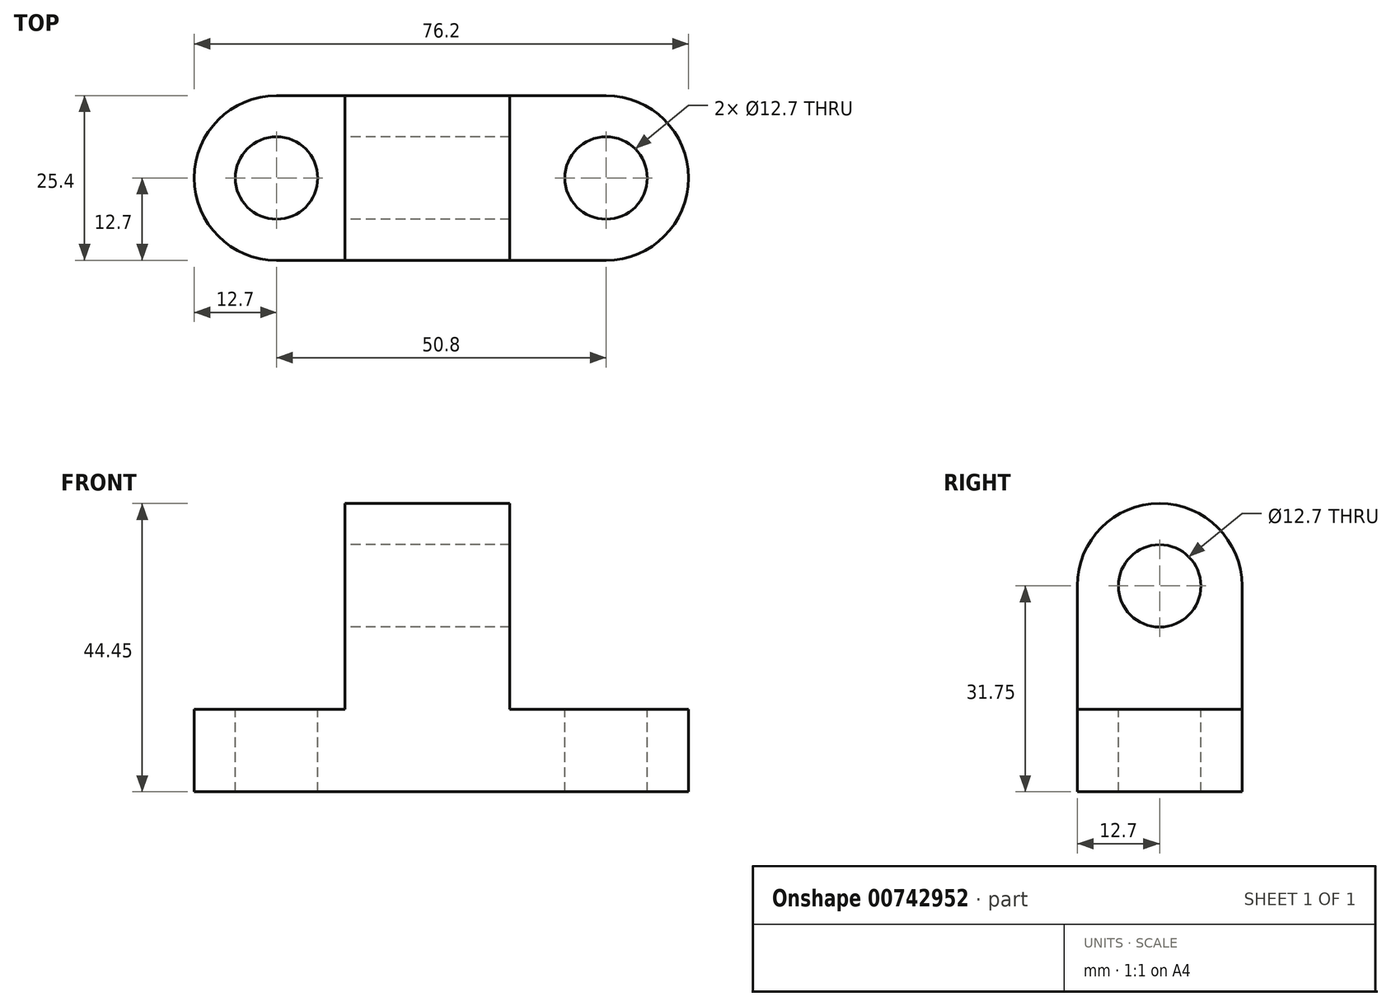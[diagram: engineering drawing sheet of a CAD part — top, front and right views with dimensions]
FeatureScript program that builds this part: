
annotation { "Feature Type Name" : "Feature", "Feature Type Description" : "" }
export const myFeature = defineFeature(function(context is Context, id is Id, definition is map)
    precondition{}
    {
        {
            var Q0;
            Q0=qCreatedBy(makeId("Front.planeOp"),FACE);
            var sketch = newSketch(context, id + "F0", { "sketchPlane" : qUnion([Q0])});
            skLineSegment(sketch, "E0.bottom", {"start": v(0, 0) * mm, "end": v(76.2, 0) * mm});
            skLineSegment(sketch, "E0.top", {"start": v(0, 57.15) * mm, "end": v(76.2, 57.15) * mm});
            skLineSegment(sketch, "E0.left", {"start": v(0, 0) * mm, "end": v(0, 57.15) * mm});
            skLineSegment(sketch, "E0.right", {"start": v(76.2, 0) * mm, "end": v(76.2, 57.15) * mm});
            skSolve(sketch);
        }
        {
            var Q0;
            Q0=makeQuery(id+"F0.imprint","IMPRINT",FACE,{"disambiguationData":[TD([[makeQuery(id+"F0.imprint","IMPRINT",EDGE,{"derivedFrom":sQuery(id+"F0.wireOp",EDGE,"E0.bottom")}),1.0]])]});
            extrude(context, id + "F1", {"entities" : qUnion([Q0]), "depth" : 25.4 * mm, "offsetDistance" : 25.4 * mm});
        }
        {
            var Q0;
            Q0=makeQuery(id+"F1.opExtrude","CAP_FACE",FACE,{"disambiguationData":[OSD([sQuery(id+"F0.wireOp",EDGE,"E0.bottom"),sQuery(id+"F0.wireOp",EDGE,"E0.top"),sQuery(id+"F0.wireOp",EDGE,"E0.left"),sQuery(id+"F0.wireOp",EDGE,"E0.right")])],"isStart":false});
            var sketch = newSketch(context, id + "F2", { "sketchPlane" : qUnion([Q0])});
            skLineSegment(sketch, "E1", {"start": v(0, 44.45) * mm, "end": v(76.2, 44.45) * mm});
            skLineSegment(sketch, "E2", {"start": v(76.2, 44.45) * mm, "end": v(76.2, 57.15) * mm});
            skLineSegment(sketch, "E3", {"start": v(76.2, 57.15) * mm, "end": v(0, 57.15) * mm});
            skLineSegment(sketch, "E4", {"start": v(0, 57.15) * mm, "end": v(0, 44.45) * mm});
            skSolve(sketch);
        }
        {
            var Q0;
            Q0 = qSketchRegion(id + "F2", true);
            extrude(context, id + "F3", {"entities" : qUnion([Q0]), "operationType" : NewBodyOperationType.REMOVE, "oppositeDirection" : true, "depth" : 25.4 * mm, "offsetDistance" : 25.4 * mm});
        }
        {
            var Q0;
            Q0=makeQuery(id+"F3.boolean.opBoolean","COPY",FACE,{"derivedFrom":makeQuery(id+"F3.opExtrude","SWEPT_FACE",FACE,{"disambiguationData":[OSD([sQuery(id+"F2.wireOp",EDGE,"E1")])]})});
            var sketch = newSketch(context, id + "F4", { "sketchPlane" : qUnion([Q0])});
            skLineSegment(sketch, "E5", {"start": v(48.66, 0) * mm, "end": v(76.2, 0) * mm});
            skLineSegment(sketch, "E6", {"start": v(76.2, 0) * mm, "end": v(76.2, -25.4) * mm});
            skLineSegment(sketch, "E7", {"start": v(76.2, -25.4) * mm, "end": v(48.66, -25.4) * mm});
            skLineSegment(sketch, "E8", {"start": v(48.66, -25.4) * mm, "end": v(48.66, 0) * mm});
            skLineSegment(sketch, "E9", {"start": v(23.26, 0) * mm, "end": v(23.26, -25.4) * mm});
            skLineSegment(sketch, "E10", {"start": v(23.26, -25.4) * mm, "end": v(0, -25.4) * mm});
            skLineSegment(sketch, "E11", {"start": v(0, -25.4) * mm, "end": v(0, 0) * mm});
            skLineSegment(sketch, "E12", {"start": v(0, 0) * mm, "end": v(23.26, 0) * mm});
            skSolve(sketch);
        }
        {
            var Q0;
            Q0=makeQuery(id+"F4.imprint","IMPRINT",FACE,{"disambiguationData":[TD([[makeQuery(id+"F4.imprint","IMPRINT",EDGE,{"derivedFrom":sQuery(id+"F4.wireOp",EDGE,"E9")}),-1.0]])]});
            var Q1;
            Q1=makeQuery(id+"F4.imprint","IMPRINT",FACE,{"disambiguationData":[TD([[makeQuery(id+"F4.imprint","IMPRINT",EDGE,{"derivedFrom":sQuery(id+"F4.wireOp",EDGE,"E5")}),-1.0]])]});
            extrude(context, id + "F5", {"entities" : qUnion([Q0, Q1]), "operationType" : NewBodyOperationType.REMOVE, "oppositeDirection" : true, "depth" : 31.75 * mm, "offsetDistance" : 25.4 * mm});
        }
        {
            var Q0;
            Q0=makeQuery(id+"F5.boolean.opBoolean","COPY",FACE,{"derivedFrom":makeQuery(id+"F5.opExtrude","CAP_FACE",FACE,{"disambiguationData":[OSD([sQuery(id+"F4.wireOp",EDGE,"E5"),sQuery(id+"F4.wireOp",EDGE,"E6"),sQuery(id+"F4.wireOp",EDGE,"E7"),sQuery(id+"F4.wireOp",EDGE,"E8")])],"isStart":false})});
            var sketch = newSketch(context, id + "F6", { "sketchPlane" : qUnion([Q0])});
            skArc(sketch, "E13", {"start": v(63.5, -25.4) * mm, "mid": v(76.2, -12.7) * mm, "end": v(63.5, 0) * mm});
            skLineSegment(sketch, "E14", {"start": v(63.5, 0) * mm, "end": v(76.2, 0) * mm});
            skLineSegment(sketch, "E15", {"start": v(76.2, 0) * mm, "end": v(76.2, -25.4) * mm});
            skLineSegment(sketch, "E16", {"start": v(76.2, -25.4) * mm, "end": v(63.5, -25.4) * mm});
            skCircle(sketch, "E17", {"center": v(63.5, -12.7) * mm, "radius": 6.35 * mm});
            skSolve(sketch);
        }
        {
            var Q0;
            Q0 = qSketchRegion(id + "F6", true);
            extrude(context, id + "F7", {"entities" : qUnion([Q0]), "operationType" : NewBodyOperationType.REMOVE, "oppositeDirection" : true, "depth" : 25.4 * mm, "offsetDistance" : 25.4 * mm});
        }
        {
            var Q0;
            Q0=makeQuery(id+"F5.boolean.opBoolean","COPY",FACE,{"derivedFrom":makeQuery(id+"F5.opExtrude","CAP_FACE",FACE,{"disambiguationData":[OSD([sQuery(id+"F4.wireOp",EDGE,"E9"),sQuery(id+"F4.wireOp",EDGE,"E10"),sQuery(id+"F4.wireOp",EDGE,"E11"),sQuery(id+"F4.wireOp",EDGE,"E12")])],"isStart":false})});
            var sketch = newSketch(context, id + "F8", { "sketchPlane" : qUnion([Q0])});
            skArc(sketch, "E18", {"start": v(12.7, 0) * mm, "mid": v(0, -12.7) * mm, "end": v(12.7, -25.4) * mm});
            skLineSegment(sketch, "E19", {"start": v(12.7, -25.4) * mm, "end": v(0, -25.4) * mm});
            skLineSegment(sketch, "E20", {"start": v(0, -25.4) * mm, "end": v(0, 0) * mm});
            skLineSegment(sketch, "E21", {"start": v(0, 0) * mm, "end": v(12.7, 0) * mm});
            skCircle(sketch, "E22", {"center": v(12.7, -12.7) * mm, "radius": 6.35 * mm});
            skSolve(sketch);
        }
        {
            var Q0;
            Q0 = qSketchRegion(id + "F8", true);
            extrude(context, id + "F9", {"entities" : qUnion([Q0]), "operationType" : NewBodyOperationType.REMOVE, "oppositeDirection" : true, "depth" : 25.4 * mm, "offsetDistance" : 25.4 * mm});
        }
        {
            var Q0;
            Q0=makeQuery(id+"F5.boolean.opBoolean","COPY",FACE,{"derivedFrom":makeQuery(id+"F5.opExtrude","SWEPT_FACE",FACE,{"disambiguationData":[OSD([sQuery(id+"F4.wireOp",EDGE,"E9")])]})});
            var sketch = newSketch(context, id + "F10", { "sketchPlane" : qUnion([Q0])});
            skArc(sketch, "E23", {"start": v(25.4, 31.75) * mm, "mid": v(12.7, 44.45) * mm, "end": v(0, 31.75) * mm});
            skCircle(sketch, "E24", {"center": v(12.7, 31.75) * mm, "radius": 6.35 * mm});
            skLineSegment(sketch, "E25", {"start": v(0, 31.75) * mm, "end": v(0, 44.45) * mm});
            skLineSegment(sketch, "E26", {"start": v(0, 44.45) * mm, "end": v(25.4, 44.45) * mm});
            skLineSegment(sketch, "E27", {"start": v(25.4, 44.45) * mm, "end": v(25.4, 31.75) * mm});
            skSolve(sketch);
        }
        {
            var Q0;
            Q0 = qSketchRegion(id + "F10", true);
            extrude(context, id + "F11", {"entities" : qUnion([Q0]), "operationType" : NewBodyOperationType.REMOVE, "oppositeDirection" : true, "depth" : 25.4 * mm, "offsetDistance" : 25.4 * mm});
        }
    });
